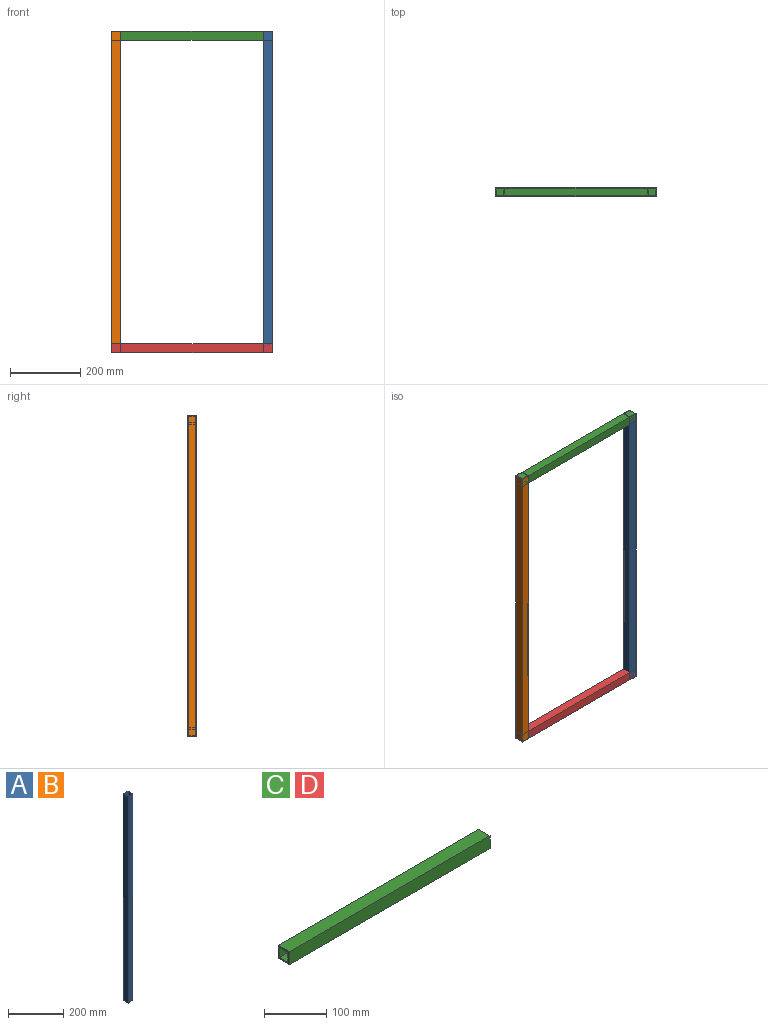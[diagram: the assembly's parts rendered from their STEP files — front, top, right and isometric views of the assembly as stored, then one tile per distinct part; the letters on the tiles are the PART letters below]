
ASSEMBLY  parts=4 mates=9
PART A: 10 faces, bbox 25.4x25.4x914.4 mm
  f0: plane 914.4x22.25mm, normal (1,0,0), area 20345.8mm2, adj f1,f7,f8,f9
  f1: plane 914.4x22.25mm, normal (0,-1,0), area 20345.8mm2, adj f0,f2,f8,f9
  f2: plane 914.4x22.25mm, normal (-1,0,0), area 20345.8mm2, adj f1,f7,f8,f9
  f3: plane 914.4x25.4mm, normal (-1,0,0), area 23225.8mm2, adj f4,f6,f8,f9
  f4: plane 914.4x25.4mm, normal (0,-1,0), area 23225.8mm2, adj f3,f5,f8,f9
  f5: plane 914.4x25.4mm, normal (1,0,0), area 23225.8mm2, adj f4,f6,f8,f9
  f6: plane 914.4x25.4mm, normal (0,1,0), area 23225.8mm2, adj f3,f5,f8,f9
  f7: plane 914.4x22.25mm, normal (0,1,0), area 20345.8mm2, adj f0,f2,f8,f9
  f8: plane 25.4x25.4mm, normal (0,0,1), area 150.1mm2, adj f0,f1,f2,f3,f4,f5,f6,f7
  f9: plane 25.4x25.4mm, normal (0,0,-1), area 150.1mm2, adj f0,f1,f2,f3,f4,f5,f6,f7
PART B: same geometry as A
PART C: 10 faces, bbox 457.2x25.4x25.4 mm
  f0: plane 457.2x19.05mm, normal (0,0,1), area 8709.7mm2, adj f1,f7,f8,f9
  f1: plane 457.2x19.05mm, normal (0,1,0), area 8709.7mm2, adj f0,f2,f8,f9
  f2: plane 457.2x19.05mm, normal (0,0,-1), area 8709.7mm2, adj f1,f7,f8,f9
  f3: plane 457.2x25.4mm, normal (0,-1,0), area 11612.9mm2, adj f4,f6,f8,f9
  f4: plane 457.2x25.4mm, normal (0,0,-1), area 11612.9mm2, adj f3,f5,f8,f9
  f5: plane 457.2x25.4mm, normal (0,1,0), area 11612.9mm2, adj f4,f6,f8,f9
  f6: plane 457.2x25.4mm, normal (0,0,1), area 11612.9mm2, adj f3,f5,f8,f9
  f7: plane 457.2x19.05mm, normal (0,-1,0), area 8709.7mm2, adj f0,f2,f8,f9
  f8: plane 25.4x25.4mm, normal (1,0,0), area 282.3mm2, adj f0,f1,f2,f3,f4,f5,f6,f7
  f9: plane 25.4x25.4mm, normal (-1,0,0), area 282.3mm2, adj f0,f1,f2,f3,f4,f5,f6,f7
PART D: same geometry as C
PLACE A t=(162.78,-62.86,-54.56)mm
PLACE B rot(axis=(-0.09,0.99,0.09),0deg) t=(-269.02,-62.86,-54.56)mm
PLACE C t=(-269.02,-62.86,834.44)mm
PLACE D rot(axis=(-0.09,0.99,0.09),0deg) t=(-269.02,-62.86,-54.56)mm
MATE planar A.f5 <-> C.f8  axis (1,0,0) through (188.18,-50.16,402.64)mm
MATE planar A.f8 <-> C.f6  axis (0,0,1) through (185.01,-40.63,859.84)mm
MATE planar B.f3 <-> D.f9  axis (-1,0,0) through (-269.02,-50.16,402.64)mm
MATE planar D.f4 <-> A.f9  axis (0,0,-1) through (-40.42,-50.16,-54.56)mm
MATE planar D.f3 <-> A.f4  axis (0,-1,0) through (188.18,-62.86,-54.56)mm
MATE planar D.f5 <-> B.f6  axis (0,1,0) through (-40.42,-37.46,-41.86)mm
MATE planar D.f4 <-> B.f9  axis (0,0,-1) through (-40.42,-50.16,-54.56)mm
MATE planar D.f8 <-> A.f5  axis (1,0,0) through (188.18,-40.63,-51.39)mm
MATE planar A.f6 <-> C.f5  axis (0,1,0) through (175.48,-37.46,859.84)mm
